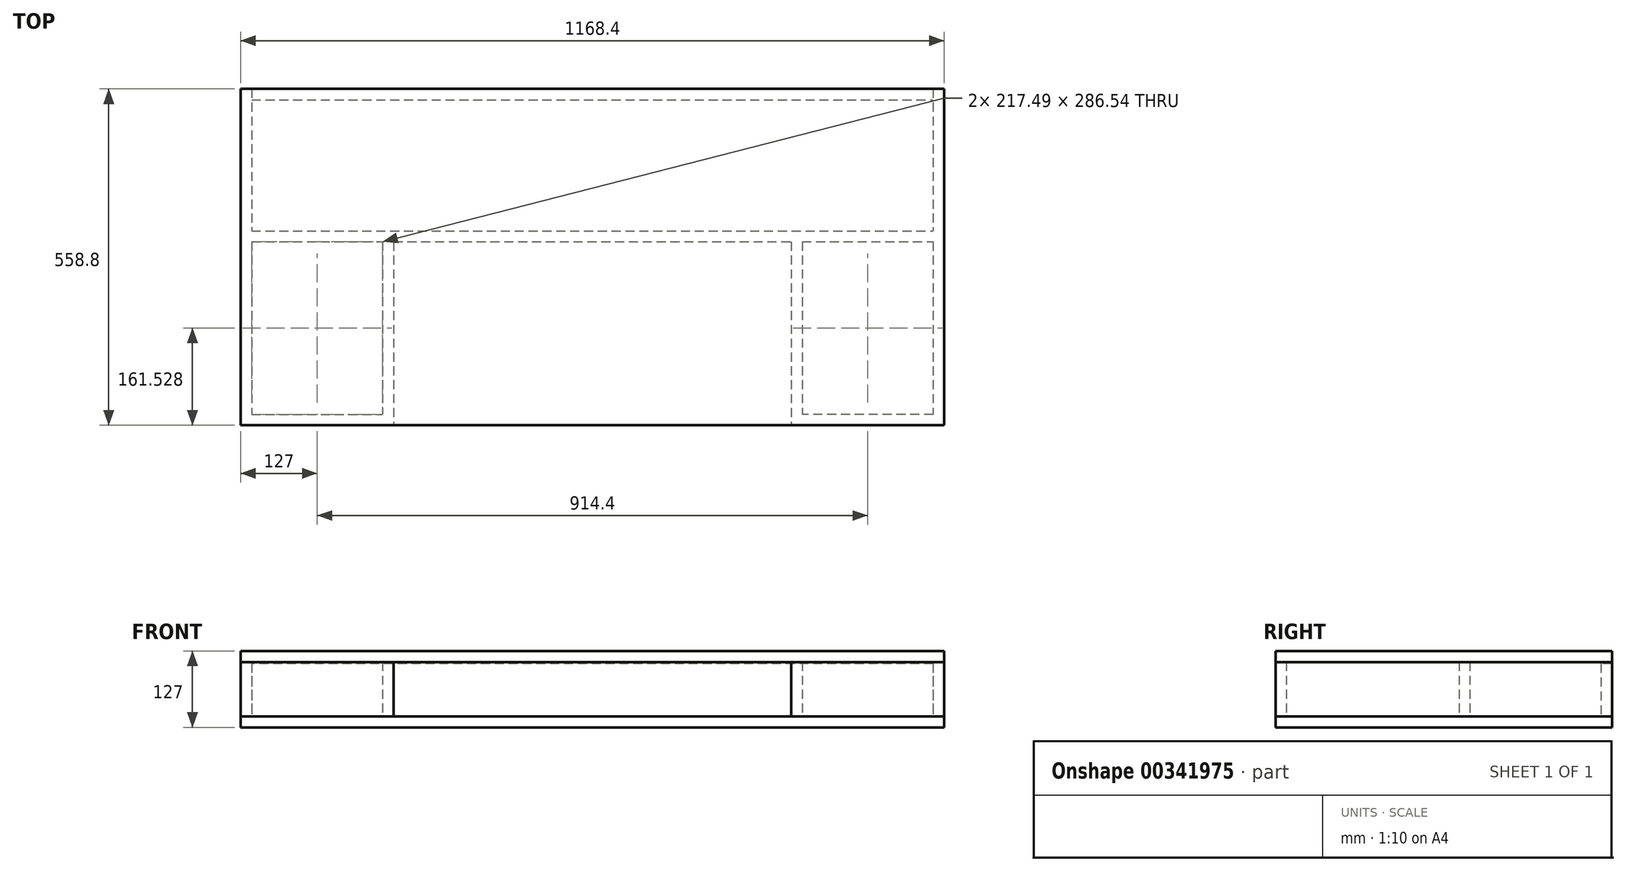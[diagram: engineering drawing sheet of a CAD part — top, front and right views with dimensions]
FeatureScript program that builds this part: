
annotation { "Feature Type Name" : "Feature", "Feature Type Description" : "" }
export const myFeature = defineFeature(function(context is Context, id is Id, definition is map)
    precondition{}
    {
        {
            var Q0;
            Q0=qCreatedBy(makeId("Top.planeOp"),FACE);
            var sketch = newSketch(context, id + "F0", { "sketchPlane" : qUnion([Q0])});
            skLineSegment(sketch, "E0.rect.bottom", {"start": v(584.2, 279.4) * mm, "end": v(-584.2, 279.4) * mm});
            skLineSegment(sketch, "E0.rect.top", {"start": v(584.2, -279.4) * mm, "end": v(-584.2, -279.4) * mm});
            skLineSegment(sketch, "E0.rect.left", {"start": v(584.2, 279.4) * mm, "end": v(584.2, -279.4) * mm});
            skLineSegment(sketch, "E0.rect.right", {"start": v(-584.2, 279.4) * mm, "end": v(-584.2, -279.4) * mm});
            skPoint(sketch, "E0.rect.middle", {"position": v(0, 0) * mm});
            skSolve(sketch);
        }
        {
            var Q0;
            Q0=qSketchRegion(id+"F0",true);
            extrude(context, id + "F1", {"entities" : qUnion([Q0]), "depth" : 18.26 * mm});
        }
        {
            var Q0;
            Q0=makeQuery(id+"F1.opExtrude","CAP_FACE",FACE,{"disambiguationData":[OSD([sQuery(id+"F0.wireOp",EDGE,"E0.rect.bottom"),sQuery(id+"F0.wireOp",EDGE,"E0.rect.top"),sQuery(id+"F0.wireOp",EDGE,"E0.rect.left"),sQuery(id+"F0.wireOp",EDGE,"E0.rect.right")])],"isStart":false});
            var sketch = newSketch(context, id + "F2", { "sketchPlane" : qUnion([Q0])});
            skLineSegment(sketch, "E1.bottom", {"start": v(-565.94, 43.66) * mm, "end": v(565.94, 43.66) * mm});
            skLineSegment(sketch, "E1.top", {"start": v(-565.94, 25.4) * mm, "end": v(565.94, 25.4) * mm});
            skLineSegment(sketch, "E1.left", {"start": v(-565.94, 43.66) * mm, "end": v(-565.94, 25.4) * mm});
            skLineSegment(sketch, "E1.right", {"start": v(565.94, 43.66) * mm, "end": v(565.94, 25.4) * mm});
            skLineSegment(sketch, "E2.rect.bottom", {"start": v(-330.2, -279.4) * mm, "end": v(330.2, -279.4) * mm, "construction": true});
            skLineSegment(sketch, "E2.rect.top", {"start": v(-330.2, 279.4) * mm, "end": v(330.2, 279.4) * mm, "construction": true});
            skLineSegment(sketch, "E2.rect.left", {"start": v(-330.2, -279.4) * mm, "end": v(-330.2, 279.4) * mm, "construction": true});
            skLineSegment(sketch, "E2.rect.right", {"start": v(330.2, -279.4) * mm, "end": v(330.2, 279.4) * mm, "construction": true});
            skPoint(sketch, "E2.rect.middle", {"position": v(0, 0) * mm});
            skPoint(sketch, "E2.rect.middle.positionSnap0", {"position": v(0, 43.66) * mm});
            skPoint(sketch, "E2.rect.centerSnap0", {"position": v(0, 43.66) * mm});
            skLineSegment(sketch, "E3.bottom", {"start": v(-330.2, 25.4) * mm, "end": v(-348.46, 25.4) * mm});
            skLineSegment(sketch, "E3.top", {"start": v(-330.2, -261.14) * mm, "end": v(-348.46, -261.14) * mm});
            skLineSegment(sketch, "E3.left", {"start": v(-330.2, 25.4) * mm, "end": v(-330.2, -261.14) * mm});
            skLineSegment(sketch, "E3.right", {"start": v(-348.46, 25.4) * mm, "end": v(-348.46, -261.14) * mm});
            skLineSegment(sketch, "E4.bottom", {"start": v(330.2, 25.4) * mm, "end": v(348.46, 25.4) * mm});
            skLineSegment(sketch, "E4.top", {"start": v(330.2, -261.14) * mm, "end": v(348.46, -261.14) * mm});
            skLineSegment(sketch, "E4.left", {"start": v(330.2, 25.4) * mm, "end": v(330.2, -261.14) * mm});
            skLineSegment(sketch, "E4.right", {"start": v(348.46, 25.4) * mm, "end": v(348.46, -261.14) * mm});
            skLineSegment(sketch, "E5.bottom", {"start": v(-584.2, 279.4) * mm, "end": v(-565.94, 279.4) * mm});
            skLineSegment(sketch, "E5.top", {"start": v(-584.2, -261.14) * mm, "end": v(-565.94, -261.14) * mm});
            skLineSegment(sketch, "E5.left", {"start": v(-584.2, 279.4) * mm, "end": v(-584.2, -261.14) * mm});
            skLineSegment(sketch, "E5.right", {"start": v(-565.94, 279.4) * mm, "end": v(-565.94, -261.14) * mm});
            skLineSegment(sketch, "E6.bottom", {"start": v(584.2, 279.4) * mm, "end": v(565.94, 279.4) * mm});
            skLineSegment(sketch, "E6.top", {"start": v(584.2, -261.14) * mm, "end": v(565.94, -261.14) * mm});
            skLineSegment(sketch, "E6.left", {"start": v(584.2, 279.4) * mm, "end": v(584.2, -261.14) * mm});
            skLineSegment(sketch, "E6.right", {"start": v(565.94, 279.4) * mm, "end": v(565.94, -261.14) * mm});
            skLineSegment(sketch, "E7.bottom", {"start": v(-584.2, -261.14) * mm, "end": v(-330.2, -261.14) * mm});
            skLineSegment(sketch, "E7.top", {"start": v(-584.2, -279.4) * mm, "end": v(-330.2, -279.4) * mm});
            skLineSegment(sketch, "E7.left", {"start": v(-584.2, -261.14) * mm, "end": v(-584.2, -279.4) * mm});
            skLineSegment(sketch, "E7.right", {"start": v(-330.2, -261.14) * mm, "end": v(-330.2, -279.4) * mm});
            skLineSegment(sketch, "E8.bottom", {"start": v(584.2, -261.14) * mm, "end": v(330.2, -261.14) * mm});
            skLineSegment(sketch, "E8.top", {"start": v(584.2, -279.4) * mm, "end": v(330.2, -279.4) * mm});
            skLineSegment(sketch, "E8.left", {"start": v(584.2, -261.14) * mm, "end": v(584.2, -279.4) * mm});
            skLineSegment(sketch, "E8.right", {"start": v(330.2, -261.14) * mm, "end": v(330.2, -279.4) * mm});
            skSolve(sketch);
        }
        {
            var Q0;
            Q0=qSketchRegion(id+"F2",true);
            extrude(context, id + "F3", {"entities" : qUnion([Q0]), "depth" : 90.49 * mm});
        }
        {
            var Q0;
            Q0=makeQuery(id+"F1.opExtrude","CAP_FACE",FACE,{"disambiguationData":[OSD([sQuery(id+"F0.wireOp",EDGE,"E0.rect.bottom"),sQuery(id+"F0.wireOp",EDGE,"E0.rect.top"),sQuery(id+"F0.wireOp",EDGE,"E0.rect.left"),sQuery(id+"F0.wireOp",EDGE,"E0.rect.right")])],"isStart":false});
            var sketch = newSketch(context, id + "F4", { "sketchPlane" : qUnion([Q0])});
            skLineSegment(sketch, "E9.bottom", {"start": v(-565.94, 279.4) * mm, "end": v(565.94, 279.4) * mm});
            skLineSegment(sketch, "E9.top", {"start": v(-565.94, 261.14) * mm, "end": v(565.94, 261.14) * mm});
            skLineSegment(sketch, "E9.left", {"start": v(-565.94, 279.4) * mm, "end": v(-565.94, 261.14) * mm});
            skLineSegment(sketch, "E9.right", {"start": v(565.94, 279.4) * mm, "end": v(565.94, 261.14) * mm});
            skSolve(sketch);
        }
        {
            var Q0;
            Q0=qSketchRegion(id+"F4",true);
            extrude(context, id + "F5", {"entities" : qUnion([Q0]), "depth" : 87.63 * mm});
        }
        {
            var Q0;
            Q0=makeQuery(id+"F3.opExtrude","CAP_FACE",FACE,{"disambiguationData":[OSD([sQuery(id+"F2.wireOp",EDGE,"E1.bottom"),sQuery(id+"F2.wireOp",EDGE,"E1.top"),sQuery(id+"F2.wireOp",EDGE,"E3.left"),sQuery(id+"F2.wireOp",EDGE,"E3.right"),sQuery(id+"F2.wireOp",EDGE,"E4.left"),sQuery(id+"F2.wireOp",EDGE,"E4.right"),sQuery(id+"F2.wireOp",EDGE,"E5.bottom"),sQuery(id+"F2.wireOp",EDGE,"E5.left"),sQuery(id+"F2.wireOp",EDGE,"E5.right"),sQuery(id+"F2.wireOp",EDGE,"E6.bottom"),sQuery(id+"F2.wireOp",EDGE,"E6.left"),sQuery(id+"F2.wireOp",EDGE,"E6.right"),sQuery(id+"F2.wireOp",EDGE,"E7.bottom"),sQuery(id+"F2.wireOp",EDGE,"E7.top"),sQuery(id+"F2.wireOp",EDGE,"E7.left"),sQuery(id+"F2.wireOp",EDGE,"E7.right"),sQuery(id+"F2.wireOp",EDGE,"E8.bottom"),sQuery(id+"F2.wireOp",EDGE,"E8.top"),sQuery(id+"F2.wireOp",EDGE,"E8.left"),sQuery(id+"F2.wireOp",EDGE,"E8.right"),sQuery(id+"F2.wireOp",EDGE,"5b780894-bd24-4c12-90cd-344abb398ec0.bottom"),sQuery(id+"F2.wireOp",EDGE,"5b780894-bd24-4c12-90cd-344abb398ec0.top")])],"isStart":false});
            var sketch = newSketch(context, id + "F6", { "sketchPlane" : qUnion([Q0])});
            skLineSegment(sketch, "E10.bottom", {"start": v(-584.2, 279.4) * mm, "end": v(584.2, 279.4) * mm});
            skLineSegment(sketch, "E10.top", {"start": v(-584.2, -279.4) * mm, "end": v(584.2, -279.4) * mm});
            skLineSegment(sketch, "E10.left", {"start": v(-584.2, 279.4) * mm, "end": v(-584.2, -279.4) * mm});
            skLineSegment(sketch, "E10.right", {"start": v(584.2, 279.4) * mm, "end": v(584.2, -279.4) * mm});
            skSolve(sketch);
        }
        {
            var Q0;
            Q0=qSketchRegion(id+"F6",true);
            extrude(context, id + "F7", {"entities" : qUnion([Q0]), "depth" : 18.26 * mm});
        }
    });
